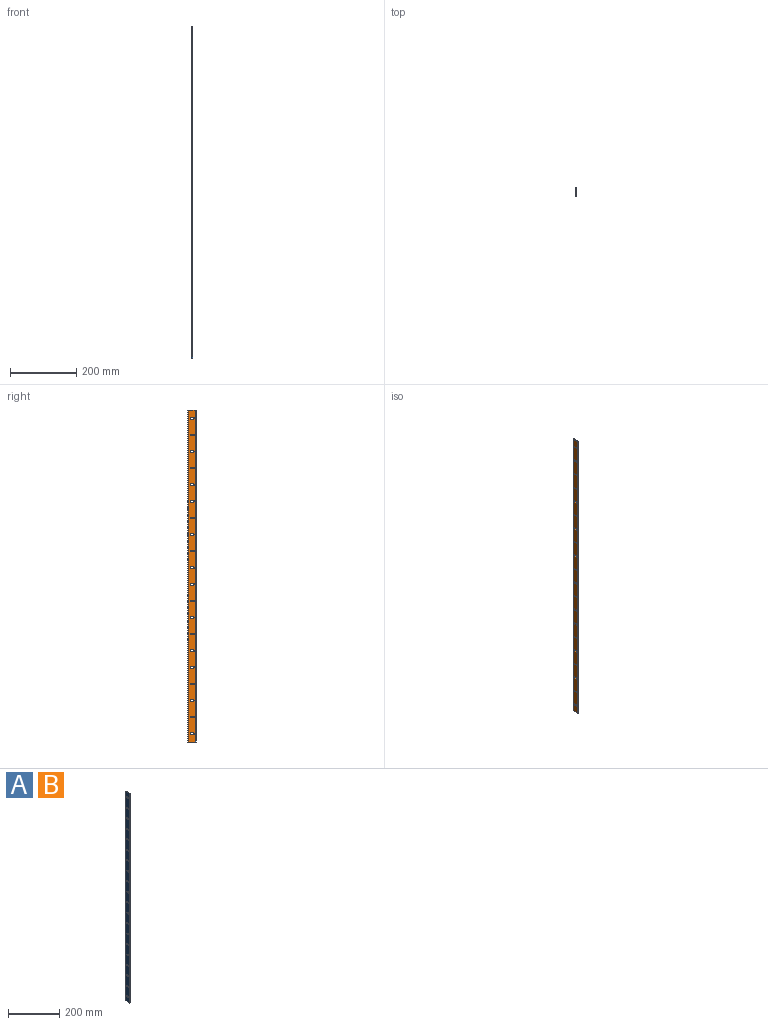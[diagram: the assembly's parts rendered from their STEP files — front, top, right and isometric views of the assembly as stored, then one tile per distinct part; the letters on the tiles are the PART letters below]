
ASSEMBLY  parts=2 mates=1
PART A: 95 faces, bbox 4.8x22.5x1000 mm
  f0: cylinder r=0.3mm len=1000mm, axis (0,0,-1), area 471.2mm2, adj f1,f12,f13,f14
  f1: plane 1000x0.28mm, normal (1,0,0), area 275mm2, adj f0,f2,f13,f14
  f2: cylinder r=0.3mm len=1000mm, axis (0,0,-1), area 235.6mm2, adj f1,f3,f13,f14
  f3: plane 1000x2.08mm, normal (0.71,0.71,0), area 2934.5mm2, adj f2,f4,f13,f14
  f4: cylinder r=0.3mm len=1000mm, axis (0,0,-1), area 471.2mm2, adj f3,f5,f13,f14
  f5: plane 1000x2.08mm, normal (-0.71,0.71,0), area 2934.5mm2, adj f4,f6,f13,f14
  f6: cylinder r=0.3mm len=1000mm, axis (0,0,-1), area 235.6mm2, adj f5,f7,f13,f14
  f7: plane 1000x19.83mm, normal (-1,0,0), area 18673.6mm2, adj f6,f8,f13,f14,f15,f16,f17,f18
  f8: cylinder r=0.3mm len=1000mm, axis (0,0,-1), area 471.2mm2, adj f7,f9,f13,f14
  f9: plane 1000x1.78mm, normal (0,-1,0), area 1775mm2, adj f8,f10,f13,f14
  f10: cylinder r=0.3mm len=1000mm, axis (0,0,-1), area 471.2mm2, adj f9,f11,f13,f14
  f11: plane 1000x19.25mm, normal (1,0,0), area 18098.6mm2, adj f10,f12,f13,f14,f15,f16,f17,f18
  f12: plane 1000x2.08mm, normal (0,-1,0), area 2075mm2, adj f0,f11,f13,f14
  f13: plane 22.5x4.75mm, normal (0,0,1), area 55.3mm2, adj f0,f1,f2,f3,f4,f5,f6,f7
  f14: plane 22.5x4.75mm, normal (0,0,-1), area 55.3mm2, adj f0,f1,f2,f3,f4,f5,f6,f7
  f15: cylinder r=2.65mm len=5.3mm, axis (1,0,0), area 19.8mm2, adj f7,f11,f16,f18
  f16: plane 6.7x2.38mm, normal (0,0,1), area 15.9mm2, adj f7,f11,f15,f17
  f17: cylinder r=2.65mm len=5.3mm, axis (1,0,0), area 19.8mm2, adj f7,f11,f16,f18
  f18: plane 6.7x2.38mm, normal (0,0,-1), area 15.9mm2, adj f7,f11,f15,f17
  f19: cylinder r=2.65mm len=5.3mm, axis (1,0,0), area 19.8mm2, adj f7,f11,f20,f22
  f20: plane 6.7x2.38mm, normal (0,0,1), area 15.9mm2, adj f7,f11,f19,f21
  f21: cylinder r=2.65mm len=5.3mm, axis (1,0,0), area 19.8mm2, adj f7,f11,f20,f22
  f22: plane 6.7x2.38mm, normal (0,0,-1), area 15.9mm2, adj f7,f11,f19,f21
  f23: plane 6.7x2.38mm, normal (0,0,-1), area 15.9mm2, adj f7,f11,f24,f26
  f24: cylinder r=2.65mm len=5.3mm, axis (1,0,0), area 19.8mm2, adj f7,f11,f23,f25
  f25: plane 6.7x2.38mm, normal (0,0,1), area 15.9mm2, adj f7,f11,f24,f26
  f26: cylinder r=2.65mm len=5.3mm, axis (1,0,0), area 19.8mm2, adj f7,f11,f23,f25
  f27: plane 6.7x2.38mm, normal (0,0,-1), area 15.9mm2, adj f7,f11,f28,f30
  f28: cylinder r=2.65mm len=5.3mm, axis (1,0,0), area 19.8mm2, adj f7,f11,f27,f29
  f29: plane 6.7x2.38mm, normal (0,0,1), area 15.9mm2, adj f7,f11,f28,f30
  f30: cylinder r=2.65mm len=5.3mm, axis (1,0,0), area 19.8mm2, adj f7,f11,f27,f29
  f31: plane 6.7x2.38mm, normal (0,0,-1), area 15.9mm2, adj f7,f11,f32,f34
  f32: cylinder r=2.65mm len=5.3mm, axis (1,0,0), area 19.8mm2, adj f7,f11,f31,f33
  f33: plane 6.7x2.38mm, normal (0,0,1), area 15.9mm2, adj f7,f11,f32,f34
  f34: cylinder r=2.65mm len=5.3mm, axis (1,0,0), area 19.8mm2, adj f7,f11,f31,f33
  f35: plane 6.7x2.38mm, normal (0,0,-1), area 15.9mm2, adj f7,f11,f36,f38
  f36: cylinder r=2.65mm len=5.3mm, axis (1,0,0), area 19.8mm2, adj f7,f11,f35,f37
  f37: plane 6.7x2.38mm, normal (0,0,1), area 15.9mm2, adj f7,f11,f36,f38
  f38: cylinder r=2.65mm len=5.3mm, axis (1,0,0), area 19.8mm2, adj f7,f11,f35,f37
  f39: plane 6.7x2.38mm, normal (0,0,-1), area 15.9mm2, adj f7,f11,f40,f42
  f40: cylinder r=2.65mm len=5.3mm, axis (1,0,0), area 19.8mm2, adj f7,f11,f39,f41
  f41: plane 6.7x2.38mm, normal (0,0,1), area 15.9mm2, adj f7,f11,f40,f42
  f42: cylinder r=2.65mm len=5.3mm, axis (1,0,0), area 19.8mm2, adj f7,f11,f39,f41
  f43: plane 6.7x2.38mm, normal (0,0,-1), area 15.9mm2, adj f7,f11,f44,f46
  f44: cylinder r=2.65mm len=5.3mm, axis (1,0,0), area 19.8mm2, adj f7,f11,f43,f45
  f45: plane 6.7x2.38mm, normal (0,0,1), area 15.9mm2, adj f7,f11,f44,f46
  f46: cylinder r=2.65mm len=5.3mm, axis (1,0,0), area 19.8mm2, adj f7,f11,f43,f45
  f47: plane 6.7x2.38mm, normal (0,0,-1), area 15.9mm2, adj f7,f11,f48,f50
  f48: cylinder r=2.65mm len=5.3mm, axis (1,0,0), area 19.8mm2, adj f7,f11,f47,f49
  f49: plane 6.7x2.38mm, normal (0,0,1), area 15.9mm2, adj f7,f11,f48,f50
  f50: cylinder r=2.65mm len=5.3mm, axis (1,0,0), area 19.8mm2, adj f7,f11,f47,f49
  f51: plane 6.7x2.38mm, normal (0,0,-1), area 15.9mm2, adj f7,f11,f52,f54
  f52: cylinder r=2.65mm len=5.3mm, axis (1,0,0), area 19.8mm2, adj f7,f11,f51,f53
  f53: plane 6.7x2.38mm, normal (0,0,1), area 15.9mm2, adj f7,f11,f52,f54
  f54: cylinder r=2.65mm len=5.3mm, axis (1,0,0), area 19.8mm2, adj f7,f11,f51,f53
  f55: plane 6.7x2.38mm, normal (0,0,-1), area 15.9mm2, adj f7,f11,f56,f58
  f56: cylinder r=2.65mm len=5.3mm, axis (1,0,0), area 19.8mm2, adj f7,f11,f55,f57
  f57: plane 6.7x2.38mm, normal (0,0,1), area 15.9mm2, adj f7,f11,f56,f58
  f58: cylinder r=2.65mm len=5.3mm, axis (1,0,0), area 19.8mm2, adj f7,f11,f55,f57
  f59: plane 6.7x2.38mm, normal (0,0,-1), area 15.9mm2, adj f7,f11,f60,f62
  f60: cylinder r=2.65mm len=5.3mm, axis (1,0,0), area 19.8mm2, adj f7,f11,f59,f61
  f61: plane 6.7x2.38mm, normal (0,0,1), area 15.9mm2, adj f7,f11,f60,f62
  f62: cylinder r=2.65mm len=5.3mm, axis (1,0,0), area 19.8mm2, adj f7,f11,f59,f61
  f63: plane 6.7x2.38mm, normal (0,0,-1), area 15.9mm2, adj f7,f11,f64,f66
  f64: cylinder r=2.65mm len=5.3mm, axis (1,0,0), area 19.8mm2, adj f7,f11,f63,f65
  f65: plane 6.7x2.38mm, normal (0,0,1), area 15.9mm2, adj f7,f11,f64,f66
  f66: cylinder r=2.65mm len=5.3mm, axis (1,0,0), area 19.8mm2, adj f7,f11,f63,f65
  f67: plane 6.7x2.38mm, normal (0,0,-1), area 15.9mm2, adj f7,f11,f68,f70
  f68: cylinder r=2.65mm len=5.3mm, axis (1,0,0), area 19.8mm2, adj f7,f11,f67,f69
  f69: plane 6.7x2.38mm, normal (0,0,1), area 15.9mm2, adj f7,f11,f68,f70
  f70: cylinder r=2.65mm len=5.3mm, axis (1,0,0), area 19.8mm2, adj f7,f11,f67,f69
  f71: plane 6.7x2.38mm, normal (0,0,-1), area 15.9mm2, adj f7,f11,f72,f74
  f72: cylinder r=2.65mm len=5.3mm, axis (1,0,0), area 19.8mm2, adj f7,f11,f71,f73
  f73: plane 6.7x2.38mm, normal (0,0,1), area 15.9mm2, adj f7,f11,f72,f74
  f74: cylinder r=2.65mm len=5.3mm, axis (1,0,0), area 19.8mm2, adj f7,f11,f71,f73
  f75: plane 6.7x2.38mm, normal (0,0,-1), area 15.9mm2, adj f7,f11,f76,f78
  f76: cylinder r=2.65mm len=5.3mm, axis (1,0,0), area 19.8mm2, adj f7,f11,f75,f77
  f77: plane 6.7x2.38mm, normal (0,0,1), area 15.9mm2, adj f7,f11,f76,f78
  f78: cylinder r=2.65mm len=5.3mm, axis (1,0,0), area 19.8mm2, adj f7,f11,f75,f77
  f79: plane 6.7x2.38mm, normal (0,0,-1), area 15.9mm2, adj f7,f11,f80,f82
  f80: cylinder r=2.65mm len=5.3mm, axis (1,0,0), area 19.8mm2, adj f7,f11,f79,f81
  f81: plane 6.7x2.38mm, normal (0,0,1), area 15.9mm2, adj f7,f11,f80,f82
  f82: cylinder r=2.65mm len=5.3mm, axis (1,0,0), area 19.8mm2, adj f7,f11,f79,f81
  f83: plane 6.7x2.38mm, normal (0,0,-1), area 15.9mm2, adj f7,f11,f84,f86
  f84: cylinder r=2.65mm len=5.3mm, axis (1,0,0), area 19.8mm2, adj f7,f11,f83,f85
  f85: plane 6.7x2.38mm, normal (0,0,1), area 15.9mm2, adj f7,f11,f84,f86
  f86: cylinder r=2.65mm len=5.3mm, axis (1,0,0), area 19.8mm2, adj f7,f11,f83,f85
  f87: plane 6.7x2.38mm, normal (0,0,-1), area 15.9mm2, adj f7,f11,f88,f90
  f88: cylinder r=2.65mm len=5.3mm, axis (1,0,0), area 19.8mm2, adj f7,f11,f87,f89
  f89: plane 6.7x2.38mm, normal (0,0,1), area 15.9mm2, adj f7,f11,f88,f90
  f90: cylinder r=2.65mm len=5.3mm, axis (1,0,0), area 19.8mm2, adj f7,f11,f87,f89
  f91: plane 6.7x2.38mm, normal (0,0,-1), area 15.9mm2, adj f7,f11,f92,f94
  f92: cylinder r=2.65mm len=5.3mm, axis (1,0,0), area 19.8mm2, adj f7,f11,f91,f93
  f93: plane 6.7x2.38mm, normal (0,0,1), area 15.9mm2, adj f7,f11,f92,f94
  f94: cylinder r=2.65mm len=5.3mm, axis (1,0,0), area 19.8mm2, adj f7,f11,f91,f93
PART B: same geometry as A
PLACE A rot(axis=(0,0,1),180deg) t=(-54.3,19.55,0)mm
PLACE B t=(-58.9,0,0)mm
MATE fastened A.f9 <-> B.f12  axis (0,1,0) through (-55.49,19.55,500)mm
